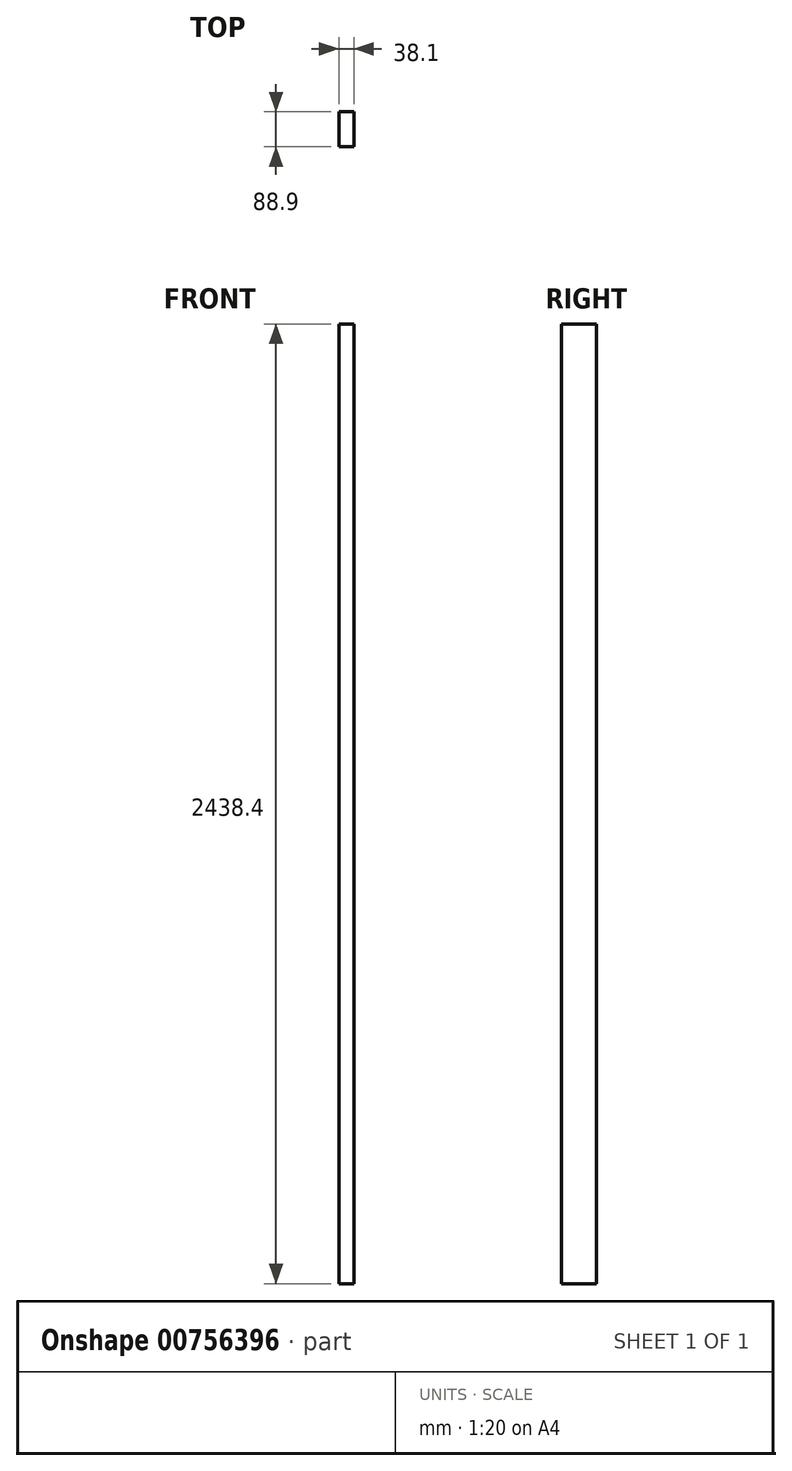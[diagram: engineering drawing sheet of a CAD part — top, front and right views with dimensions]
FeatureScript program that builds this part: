
annotation { "Feature Type Name" : "Feature", "Feature Type Description" : "" }
export const myFeature = defineFeature(function(context is Context, id is Id, definition is map)
    precondition{}
    {
        {
            var Q0;
            Q0=qCreatedBy(makeId("Top.planeOp"),FACE);
            var sketch = newSketch(context, id + "F0", { "sketchPlane" : qUnion([Q0])});
            skLineSegment(sketch, "E0.bottom", {"start": v(0, 88.9) * mm, "end": v(38.1, 88.9) * mm});
            skLineSegment(sketch, "E0.top", {"start": v(0, 0) * mm, "end": v(38.1, 0) * mm});
            skLineSegment(sketch, "E0.left", {"start": v(0, 88.9) * mm, "end": v(0, 0) * mm});
            skLineSegment(sketch, "E0.right", {"start": v(38.1, 88.9) * mm, "end": v(38.1, 0) * mm});
            skPoint(sketch, "E1.visualSharp", {"position": v(0, 88.9) * mm});
            skPoint(sketch, "E2.visualSharp", {"position": v(38.1, 88.9) * mm});
            skPoint(sketch, "E3.visualSharp", {"position": v(0, 0) * mm});
            skPoint(sketch, "E4.visualSharp", {"position": v(38.1, 0) * mm});
            skSolve(sketch);
        }
        {
            var Q0;
            Q0=makeQuery(id+"F0.imprint","IMPRINT",FACE,{"disambiguationData":[TD([[makeQuery(id+"F0.imprint","IMPRINT",EDGE,{"derivedFrom":sQuery(id+"F0.wireOp",EDGE,"E0.bottom")}),-1.0]])]});
            extrude(context, id + "F1", {"entities" : qUnion([Q0]), "depth" : 2438.4 * mm, "offsetDistance" : 30.48 * mm});
        }
    });
